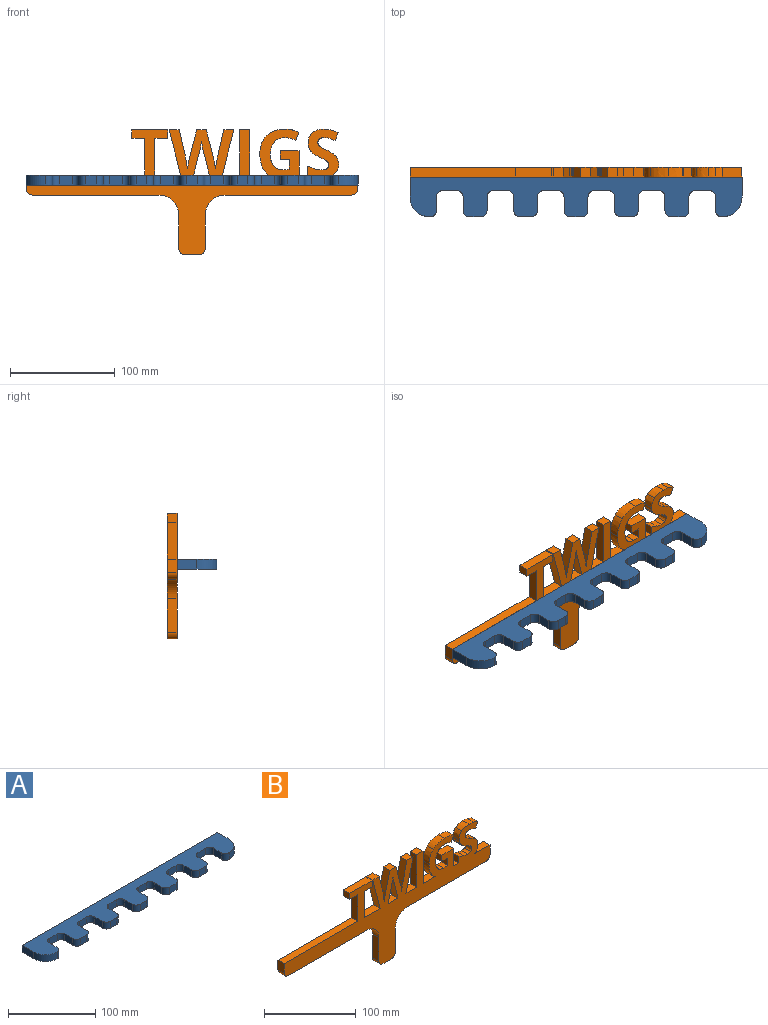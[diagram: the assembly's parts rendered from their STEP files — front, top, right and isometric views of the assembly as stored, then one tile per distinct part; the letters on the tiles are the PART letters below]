
ASSEMBLY  parts=2 mates=1
PART A: 54 faces, bbox 317.5x38.1x9.5 mm
  f0: cylinder r=6.35mm len=9.53mm, axis (0,0,-1), area 95mm2, adj f1,f51,f52,f53
  f1: plane 12.7x9.53mm, normal (0,-1,0), area 121mm2, adj f0,f2,f52,f53
  f2: cylinder r=6.35mm len=9.53mm, axis (0,0,-1), area 95mm2, adj f1,f3,f52,f53
  f3: plane 12.7x9.53mm, normal (-1,0,0), area 121mm2, adj f2,f4,f52,f53
  f4: cylinder r=6.35mm len=9.53mm, axis (0,0,-1), area 95mm2, adj f3,f5,f52,f53
  f5: plane 10.16x9.53mm, normal (0,-1,0), area 96.8mm2, adj f4,f6,f52,f53
  f6: cylinder r=6.35mm len=9.53mm, axis (0,0,-1), area 95mm2, adj f5,f7,f52,f53
  f7: plane 12.7x9.53mm, normal (1,0,0), area 121mm2, adj f6,f8,f52,f53
  f8: cylinder r=6.35mm len=9.53mm, axis (0,0,-1), area 95mm2, adj f7,f9,f52,f53
  f9: plane 12.7x9.53mm, normal (0,-1,0), area 121mm2, adj f8,f10,f52,f53
  f10: cylinder r=6.35mm len=9.53mm, axis (0,0,-1), area 95mm2, adj f9,f11,f52,f53
  f11: plane 12.7x9.53mm, normal (-1,0,0), area 121mm2, adj f10,f12,f52,f53
  f12: cylinder r=6.35mm len=9.53mm, axis (0,0,-1), area 95mm2, adj f11,f13,f52,f53
  f13: plane 10.16x9.53mm, normal (0,-1,0), area 96.8mm2, adj f12,f14,f52,f53
  f14: cylinder r=6.35mm len=9.53mm, axis (0,0,-1), area 95mm2, adj f13,f15,f52,f53
  f15: plane 12.7x9.53mm, normal (1,0,0), area 121mm2, adj f14,f16,f52,f53
  f16: cylinder r=6.35mm len=9.53mm, axis (0,0,-1), area 95mm2, adj f15,f17,f52,f53
  f17: plane 12.7x9.53mm, normal (0,-1,0), area 121mm2, adj f16,f18,f52,f53
  f18: cylinder r=6.35mm len=9.53mm, axis (0,0,-1), area 95mm2, adj f17,f19,f52,f53
  f19: plane 12.7x9.53mm, normal (-1,0,0), area 121mm2, adj f18,f20,f52,f53
  f20: cylinder r=6.35mm len=9.53mm, axis (0,0,-1), area 95mm2, adj f19,f21,f52,f53
  f21: plane 10.16x9.53mm, normal (0,-1,0), area 96.8mm2, adj f20,f22,f52,f53
  f22: cylinder r=6.35mm len=9.53mm, axis (0,0,-1), area 95mm2, adj f21,f23,f52,f53
  f23: plane 12.7x9.53mm, normal (1,0,0), area 121mm2, adj f22,f24,f52,f53
  f24: cylinder r=6.35mm len=9.53mm, axis (0,0,-1), area 95mm2, adj f23,f25,f52,f53
  f25: plane 12.7x9.53mm, normal (0,-1,0), area 121mm2, adj f24,f26,f52,f53
  f26: cylinder r=6.35mm len=9.53mm, axis (0,0,-1), area 95mm2, adj f25,f27,f52,f53
  f27: plane 12.7x9.53mm, normal (-1,0,0), area 121mm2, adj f26,f28,f52,f53
  f28: cylinder r=6.35mm len=9.53mm, axis (0,0,-1), area 95mm2, adj f27,f29,f52,f53
  f29: plane 10.16x9.53mm, normal (0,-1,0), area 96.8mm2, adj f28,f30,f52,f53
  f30: cylinder r=6.35mm len=9.53mm, axis (0,0,-1), area 95mm2, adj f29,f31,f52,f53
  f31: plane 12.7x9.53mm, normal (1,0,0), area 121mm2, adj f30,f32,f52,f53
  f32: cylinder r=6.35mm len=9.53mm, axis (0,0,-1), area 95mm2, adj f31,f33,f52,f53
  f33: plane 12.7x9.53mm, normal (0,-1,0), area 121mm2, adj f32,f34,f52,f53
  f34: cylinder r=6.35mm len=9.53mm, axis (0,0,-1), area 95mm2, adj f33,f35,f52,f53
  f35: plane 12.7x9.53mm, normal (-1,0,0), area 121mm2, adj f34,f36,f52,f53
  f36: cylinder r=6.35mm len=9.53mm, axis (0,0,-1), area 95mm2, adj f35,f37,f52,f53
  f37: plane 10.16x9.53mm, normal (0,-1,0), area 96.8mm2, adj f36,f38,f52,f53
  f38: cylinder r=6.35mm len=9.53mm, axis (0,0,-1), area 95mm2, adj f37,f39,f52,f53
  f39: plane 12.7x9.53mm, normal (1,0,0), area 121mm2, adj f38,f40,f52,f53
  f40: cylinder r=6.35mm len=9.53mm, axis (0,0,-1), area 95mm2, adj f39,f41,f52,f53
  f41: plane 12.7x9.53mm, normal (0,-1,0), area 121mm2, adj f40,f42,f52,f53
  f42: cylinder r=6.35mm len=9.53mm, axis (0,0,-1), area 95mm2, adj f41,f43,f52,f53
  f43: plane 12.7x9.53mm, normal (-1,0,0), area 121mm2, adj f42,f44,f52,f53
  f44: cylinder r=6.35mm len=9.53mm, axis (0,0,-1), area 95mm2, adj f43,f45,f52,f53
  f45: cylinder r=19.05mm len=19.05mm, axis (0,0,-1), area 285mm2, adj f44,f46,f52,f53
  f46: plane 19.05x9.53mm, normal (1,0,0), area 181.5mm2, adj f45,f47,f52,f53
  f47: plane 317.5x9.53mm, normal (0,1,0), area 3024.2mm2, adj f46,f48,f52,f53
  f48: plane 19.05x9.53mm, normal (-1,0,0), area 181.5mm2, adj f47,f49,f52,f53
  f49: cylinder r=19.05mm len=19.05mm, axis (0,0,-1), area 285mm2, adj f48,f50,f52,f53
  f50: cylinder r=6.35mm len=9.53mm, axis (0,0,-1), area 95mm2, adj f49,f51,f52,f53
  f51: plane 12.7x9.53mm, normal (1,0,0), area 121mm2, adj f0,f50,f52,f53
  f52: plane 317.5x38.1mm, normal (0,0,1), area 8070mm2, adj f0,f1,f2,f3,f4,f5,f6,f7
  f53: plane 317.5x38.1mm, normal (0,0,-1), area 8070mm2, adj f0,f1,f2,f3,f4,f5,f6,f7
PART B: 98 faces, bbox 317.5x9.5x120.1 mm
  f0: plane 21.55x9.53mm, normal (-0.97,0,-0.25), area 211.9mm2, adj f1,f95,f96,f97
  f1: plane 15.29x9.53mm, normal (0,0,1), area 145.7mm2, adj f0,f2,f96,f97
  f2: plane 21.49x9.53mm, normal (0.97,0,-0.25), area 211.3mm2, adj f1,f3,f96,f97
  f3: extruded ~9.53x5.32mm, area 51.9mm2, adj f2,f4,f96,f97
  f4: extruded ~9.53x5.42mm, area 52.4mm2, adj f3,f5,f96,f97
  f5: extruded ~9.53x5.39mm, area 52.2mm2, adj f4,f95,f96,f97
  f6: plane 23.2x9.53mm, normal (1,0,0), area 221mm2, adj f7,f94,f96,f97
  f7: plane 18.12x9.53mm, normal (0,0,1), area 172.6mm2, adj f6,f8,f96,f97
  f8: plane 9.53x8.06mm, normal (-1,0,0), area 76.8mm2, adj f7,f9,f96,f97
  f9: plane 9.53x8.65mm, normal (0,0,-1), area 82.4mm2, adj f8,f10,f96,f97
  f10: plane 9.53x9.52mm, normal (-1,0,0), area 90.7mm2, adj f9,f11,f96,f97
  f11: extruded ~9.53x6.16mm, area 59mm2, adj f10,f12,f96,f97
  f12: extruded ~9.53x8.85mm, area 95.7mm2, adj f11,f13,f96,f97
  f13: extruded ~11.35x9.53mm, area 114mm2, adj f12,f14,f96,f97
  f14: extruded ~11.33x9.53mm, area 116.4mm2, adj f13,f15,f96,f97
  f15: extruded ~10.05x9.53mm, area 107.2mm2, adj f14,f16,f96,f97
  f16: extruded ~10.4x9.53mm, area 102.8mm2, adj f15,f17,f96,f97
  f17: plane 9.53x7.74mm, normal (0.92,0,-0.38), area 79.9mm2, adj f16,f18,f96,f97
  f18: extruded ~13.56x9.53mm, area 132.8mm2, adj f17,f19,f96,f97
  f19: extruded ~17.53x9.53mm, area 181.7mm2, adj f18,f20,f96,f97
  f20: extruded ~17.23x9.53mm, area 179.8mm2, adj f19,f21,f96,f97
  f21: extruded ~17.45x9.53mm, area 178.1mm2, adj f20,f22,f96,f97
  f22: extruded ~9.53x3.57mm, area 44.6mm2, adj f21,f23,f96,f97
  f23: plane 18.48x9.53mm, normal (0,0,1), area 176mm2, adj f22,f24,f96,f97
  f24: plane 43.22x9.53mm, normal (1,0,0), area 411.7mm2, adj f23,f25,f96,f97
  f25: plane 9.68x9.53mm, normal (0,0,1), area 92.2mm2, adj f24,f26,f96,f97
  f26: plane 43.22x9.53mm, normal (-1,0,0), area 411.7mm2, adj f25,f27,f96,f97
  f27: plane 16.75x9.53mm, normal (0,0,1), area 159.5mm2, adj f26,f28,f96,f97
  f28: plane 43.22x11mm, normal (0.97,0,-0.25), area 424.8mm2, adj f27,f29,f96,f97
  f29: plane 9.53x9.53mm, normal (0,0,1), area 90.8mm2, adj f28,f30,f96,f97
  f30: plane 24.92x9.53mm, normal (-0.97,0,0.23), area 243.7mm2, adj f29,f31,f96,f97
  f31: extruded ~9.53x5.89mm, area 57.3mm2, adj f30,f32,f96,f97
  f32: extruded ~9.53x6.08mm, area 58.7mm2, adj f31,f33,f96,f97
  f33: extruded ~9.53x6.06mm, area 58.5mm2, adj f32,f34,f96,f97
  f34: extruded ~9.53x5.24mm, area 51mm2, adj f33,f35,f96,f97
  f35: plane 25.58x9.53mm, normal (0.97,0,0.25), area 251.8mm2, adj f34,f36,f96,f97
  f36: plane 9.53x9.14mm, normal (0,0,1), area 87.1mm2, adj f35,f37,f96,f97
  f37: plane 25.58x9.53mm, normal (-0.97,0,0.25), area 251.8mm2, adj f36,f38,f96,f97
  f38: extruded ~9.53x5.79mm, area 56.5mm2, adj f37,f39,f96,f97
  f39: extruded ~9.53x5.51mm, area 53.1mm2, adj f38,f40,f96,f97
  f40: extruded ~11.96x9.53mm, area 115.9mm2, adj f39,f41,f96,f97
  f41: plane 24.92x9.53mm, normal (0.97,0,0.23), area 243.8mm2, adj f40,f42,f96,f97
  f42: plane 9.53x9.52mm, normal (0,0,1), area 90.7mm2, adj f41,f43,f96,f97
  f43: plane 43.22x11.03mm, normal (-0.97,0,-0.25), area 424.9mm2, adj f42,f44,f96,f97
  f44: plane 24.7x9.53mm, normal (0,0,1), area 235.3mm2, adj f43,f45,f96,f97
  f45: plane 35.17x9.53mm, normal (1,0,0), area 335mm2, adj f44,f46,f96,f97
  f46: plane 12.39x9.53mm, normal (0,0,-1), area 118mm2, adj f45,f47,f96,f97
  f47: plane 9.53x8.05mm, normal (1,0,0), area 76.7mm2, adj f46,f48,f96,f97
  f48: plane 34.48x9.53mm, normal (0,0,1), area 328.4mm2, adj f47,f49,f96,f97
  f49: plane 9.53x8.05mm, normal (-1,0,0), area 76.7mm2, adj f48,f50,f96,f97
  f50: plane 12.4x9.53mm, normal (0,0,-1), area 118.1mm2, adj f49,f51,f96,f97
  f51: plane 35.17x9.53mm, normal (-1,0,0), area 335mm2, adj f50,f52,f96,f97
  f52: plane 113.56x9.53mm, normal (0,0,1), area 1081.7mm2, adj f51,f53,f96,f97
  f53: plane 12.7x9.53mm, normal (-1,0,0), area 121mm2, adj f52,f54,f96,f97
  f54: cylinder r=6.35mm len=9.53mm, axis (0,1,0), area 95mm2, adj f53,f55,f96,f97
  f55: plane 120.65x9.53mm, normal (0,0,-1), area 1149.2mm2, adj f54,f56,f96,f97
  f56: cylinder r=19.05mm len=19.05mm, axis (0,1,0), area 285mm2, adj f55,f57,f96,f97
  f57: plane 31.75x9.53mm, normal (-1,0,0), area 302.4mm2, adj f56,f58,f96,f97
  f58: cylinder r=6.35mm len=9.53mm, axis (0,1,0), area 95mm2, adj f57,f59,f96,f97
  f59: plane 12.7x9.53mm, normal (0,0,-1), area 121mm2, adj f58,f60,f96,f97
  f60: cylinder r=6.35mm len=9.53mm, axis (0,1,0), area 95mm2, adj f59,f61,f96,f97
  f61: plane 31.75x9.53mm, normal (1,0,0), area 302.4mm2, adj f60,f62,f96,f97
  f62: cylinder r=19.05mm len=19.05mm, axis (0,1,0), area 285mm2, adj f61,f63,f96,f97
  f63: plane 120.65x9.53mm, normal (0,0,-1), area 1149.2mm2, adj f62,f64,f96,f97
  f64: cylinder r=6.35mm len=9.53mm, axis (0,1,0), area 95mm2, adj f63,f65,f96,f97
  f65: plane 12.7x9.53mm, normal (1,0,0), area 121mm2, adj f64,f66,f96,f97
  f66: plane 23.68x9.53mm, normal (0,0,1), area 225.5mm2, adj f65,f67,f96,f97
  f67: extruded ~9.53x0.66mm, area 7.9mm2, adj f66,f68,f96,f97
  f68: extruded ~9.75x9.53mm, area 105.9mm2, adj f67,f69,f96,f97
  f69: extruded ~9.53x7.54mm, area 76.7mm2, adj f68,f70,f96,f97
  f70: extruded ~9.53x8.78mm, area 102.9mm2, adj f69,f71,f96,f97
  f71: extruded ~9.53x6.13mm, area 65.9mm2, adj f70,f72,f96,f97
  f72: extruded ~9.53x1.89mm, area 25.3mm2, adj f71,f73,f96,f97
  f73: extruded ~9.53x2.23mm, area 22.3mm2, adj f72,f74,f96,f97
  f74: extruded ~9.53x3.34mm, area 35.9mm2, adj f73,f75,f96,f97
  f75: extruded ~9.53x4.22mm, area 42.9mm2, adj f74,f76,f96,f97
  f76: extruded ~9.53x4.7mm, area 45.2mm2, adj f75,f77,f96,f97
  f77: extruded ~9.53x6.05mm, area 61mm2, adj f76,f78,f96,f97
  f78: plane 9.53x7.54mm, normal (0.92,0,-0.38), area 77.7mm2, adj f77,f79,f96,f97
  f79: extruded ~9.53x6.76mm, area 68.3mm2, adj f78,f80,f96,f97
  f80: extruded ~9.53x6.79mm, area 65.3mm2, adj f79,f81,f96,f97
  f81: extruded ~11.35x9.53mm, area 115.4mm2, adj f80,f82,f96,f97
  f82: extruded ~9.53x9.53mm, area 102.3mm2, adj f81,f83,f96,f97
  f83: extruded ~9.53x5.62mm, area 55.3mm2, adj f82,f84,f96,f97
  f84: extruded ~9.53x4.22mm, area 51.6mm2, adj f83,f85,f96,f97
  f85: extruded ~9.53x6.27mm, area 69.9mm2, adj f84,f86,f96,f97
  f86: extruded ~9.53x5.92mm, area 63.7mm2, adj f85,f87,f96,f97
  f87: extruded ~9.53x2.2mm, area 28.6mm2, adj f86,f88,f96,f97
  f88: extruded ~9.53x2.39mm, area 24.2mm2, adj f87,f89,f96,f97
  f89: extruded ~9.53x3.62mm, area 39.7mm2, adj f88,f90,f96,f97
  f90: extruded ~9.53x4.88mm, area 48.7mm2, adj f89,f91,f96,f97
  f91: extruded ~9.53x5.86mm, area 56.5mm2, adj f90,f92,f96,f97
  f92: extruded ~9.53x7.82mm, area 79.6mm2, adj f91,f93,f96,f97
  f93: plane 9.53x8.68mm, normal (-1,0,0), area 82.7mm2, adj f92,f94,f96,f97
  f94: plane 9.53x8.05mm, normal (0,0,1), area 76.7mm2, adj f6,f93,f96,f97
  f95: extruded ~9.53x5.29mm, area 51.6mm2, adj f0,f5,f96,f97
  f96: plane 317.5x120.07mm, normal (0,-1,0), area 11728.9mm2, adj f0,f1,f2,f3,f4,f5,f6,f7
  f97: plane 317.5x120.07mm, normal (0,1,0), area 11728.9mm2, adj f0,f1,f2,f3,f4,f5,f6,f7
PLACE A t=(19.34,3.48,21.31)mm
PLACE B t=(19.34,25.71,-7.27)mm
MATE fastened A.f47 <-> B.f96  axis (0,1,0) through (178.09,16.18,30.83)mm
